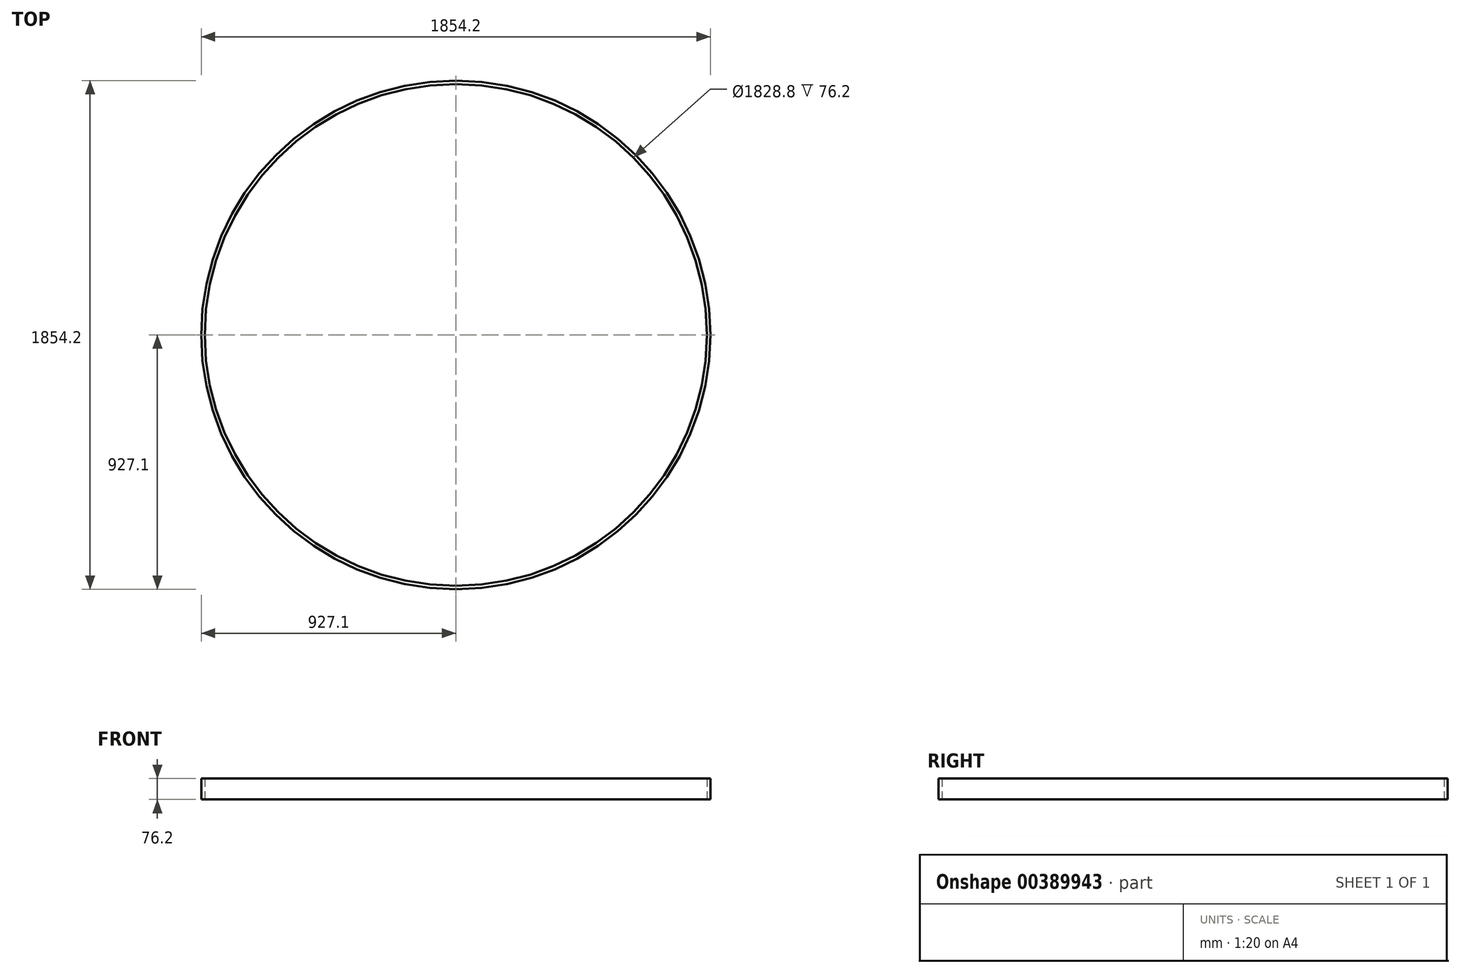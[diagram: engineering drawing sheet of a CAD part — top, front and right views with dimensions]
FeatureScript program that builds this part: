
annotation { "Feature Type Name" : "Feature", "Feature Type Description" : "" }
export const myFeature = defineFeature(function(context is Context, id is Id, definition is map)
    precondition{}
    {
        {
            var Q0;
            Q0=qCreatedBy(makeId("Top.planeOp"),FACE);
            var sketch = newSketch(context, id + "F0", { "sketchPlane" : qUnion([Q0])});
            skCircle(sketch, "E0", {"center": v(0, 0) * mm, "radius": 914.4 * mm});
            skCircle(sketch, "E1", {"center": v(0, 0) * mm, "radius": 927.1 * mm});
            skSolve(sketch);
        }
        {
            var Q0;
            Q0 = qSketchRegion(id + "F0", true);
            extrude(context, id + "F1", {"entities" : qUnion([Q0]), "depth" : 76.2 * mm});
        }
    });
